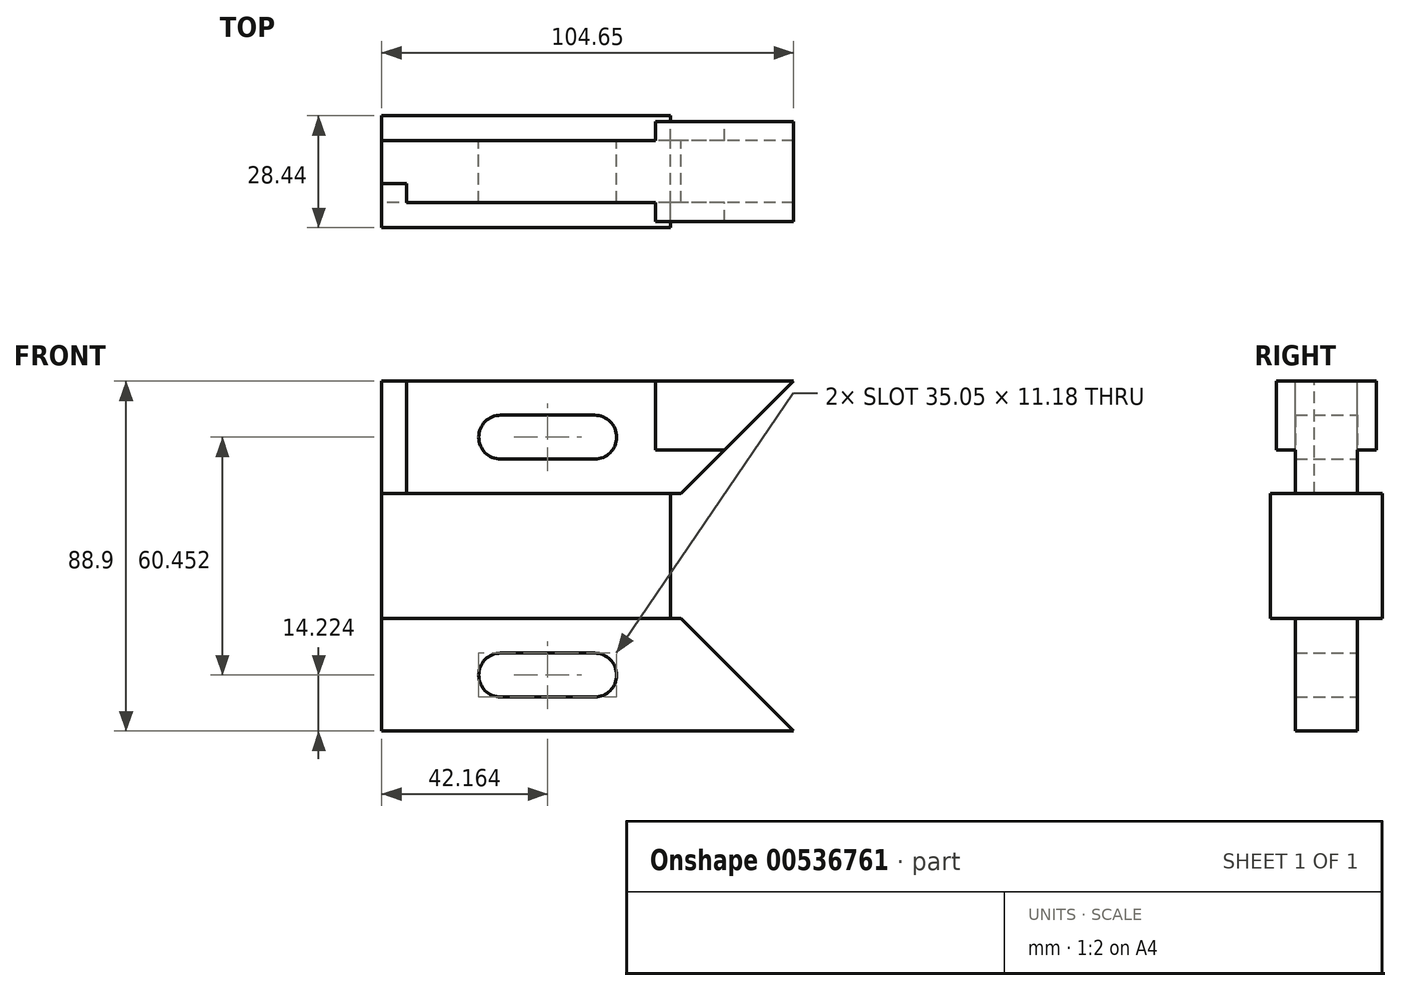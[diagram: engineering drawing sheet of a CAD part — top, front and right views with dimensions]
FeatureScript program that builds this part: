
annotation { "Feature Type Name" : "Feature", "Feature Type Description" : "" }
export const myFeature = defineFeature(function(context is Context, id is Id, definition is map)
    precondition{}
    {
        {
            var Q0;
            Q0=qCreatedBy(makeId("Right.planeOp"),FACE);
            var sketch = newSketch(context, id + "F0", { "sketchPlane" : qUnion([Q0])});
            skLineSegment(sketch, "E0.bottom", {"start": v(-14.22, 15.88) * mm, "end": v(14.22, 15.88) * mm});
            skLineSegment(sketch, "E0.top", {"start": v(-14.22, -15.87) * mm, "end": v(14.22, -15.87) * mm});
            skLineSegment(sketch, "E0.left", {"start": v(-14.22, 15.88) * mm, "end": v(-14.22, -15.87) * mm});
            skLineSegment(sketch, "E0.right", {"start": v(14.22, 15.88) * mm, "end": v(14.22, -15.87) * mm});
            skPoint(sketch, "E0.middle", {"position": v(0, 0) * mm});
            skSolve(sketch);
        }
        {
            var Q0;
            Q0 = qSketchRegion(id + "F0", true);
            extrude(context, id + "F1", {"entities" : qUnion([Q0]), "depth" : 73.4 * mm, "offsetDistance" : 25.4 * mm});
        }
        {
            var Q0;
            Q0=qCreatedBy(makeId("Front.planeOp"),FACE);
            var sketch = newSketch(context, id + "F2", { "sketchPlane" : qUnion([Q0])});
            skLineSegment(sketch, "E1.0", {"start": v(76.07, 15.88) * mm, "end": v(0, 15.88) * mm});
            skLineSegment(sketch, "E2", {"start": v(0, 15.88) * mm, "end": v(0, 44.45) * mm});
            skLineSegment(sketch, "E3", {"start": v(0, 44.45) * mm, "end": v(104.65, 44.45) * mm});
            skLineSegment(sketch, "E4", {"start": v(104.65, 44.45) * mm, "end": v(76.07, 15.87) * mm});
            skPoint(sketch, "E5.centerSnap1", {"position": v(36.7, 15.88) * mm});
            skCircle(sketch, "E6", {"center": v(30.23, 30.23) * mm, "radius": 5.59 * mm});
            skCircle(sketch, "E7", {"center": v(54.1, 30.23) * mm, "radius": 5.59 * mm});
            skLineSegment(sketch, "E8", {"start": v(30.23, 35.81) * mm, "end": v(54.1, 35.81) * mm});
            skLineSegment(sketch, "E9", {"start": v(30.23, 24.64) * mm, "end": v(54.1, 24.64) * mm});
            skLineSegment(sketch, "E10.MirrorCS", {"start": v(0, -15.88) * mm, "end": v(0, -44.45) * mm});
            skLineSegment(sketch, "E11.MirrorCS", {"start": v(0, -44.45) * mm, "end": v(104.65, -44.45) * mm});
            skLineSegment(sketch, "E12.MirrorCS", {"start": v(104.65, -44.45) * mm, "end": v(76.07, -15.87) * mm});
            skCircle(sketch, "E13.MirrorC", {"center": v(54.1, -30.23) * mm, "radius": 5.59 * mm});
            skLineSegment(sketch, "E14.MirrorCS", {"start": v(30.23, -35.81) * mm, "end": v(54.1, -35.81) * mm});
            skCircle(sketch, "E15.MirrorC", {"center": v(30.23, -30.23) * mm, "radius": 5.59 * mm});
            skLineSegment(sketch, "E16.MirrorCS", {"start": v(30.23, -24.64) * mm, "end": v(54.1, -24.64) * mm});
            skPoint(sketch, "E17.orphan", {"position": v(73.4, 15.88) * mm});
            skLineSegment(sketch, "E18.MirrorCS", {"start": v(76.07, -15.88) * mm, "end": v(0, -15.88) * mm});
            skSolve(sketch);
        }
        {
            var Q0;
            Q0=makeQuery(id+"F2.imprint","IMPRINT",FACE,{"disambiguationData":[TD([[makeQuery(id+"F2.imprint","IMPRINT",EDGE,{"derivedFrom":sQuery(id+"F2.wireOp",EDGE,"E1.0")}),-1.0]])]});
            var Q1;
            Q1=makeQuery(id+"F2.imprint","IMPRINT",FACE,{"disambiguationData":[TD([[makeQuery(id+"F2.imprint","IMPRINT",EDGE,{"derivedFrom":sQuery(id+"F2.wireOp",EDGE,"E10.MirrorCS")}),1.0]])]});
            extrude(context, id + "F3", {"entities" : qUnion([Q0, Q1]), "operationType" : NewBodyOperationType.ADD, "endBound" : BoundingType.SYMMETRIC, "depth" : 15.75 * mm, "offsetDistance" : 25.4 * mm});
        }
        {
            var Q0;
            Q0=makeQuery(id+"F3.opExtrude","CAP_FACE",FACE,{"disambiguationData":[OSD([sQuery(id+"F2.wireOp",EDGE,"E1.0"),sQuery(id+"F2.wireOp",EDGE,"E2"),sQuery(id+"F2.wireOp",EDGE,"E3"),sQuery(id+"F2.wireOp",EDGE,"E4"),sQuery(id+"F2.wireOp",EDGE,"E6"),sQuery(id+"F2.wireOp",EDGE,"E7"),sQuery(id+"F2.wireOp",EDGE,"E8"),sQuery(id+"F2.wireOp",EDGE,"E9")])],"isStart":false});
            var sketch = newSketch(context, id + "F4", { "sketchPlane" : qUnion([Q0])});
            skLineSegment(sketch, "E19.bottom", {"start": v(0, 15.88) * mm, "end": v(6.35, 15.88) * mm});
            skLineSegment(sketch, "E19.top", {"start": v(0, 44.45) * mm, "end": v(6.35, 44.45) * mm});
            skLineSegment(sketch, "E19.left", {"start": v(0, 15.88) * mm, "end": v(0, 44.45) * mm});
            skLineSegment(sketch, "E19.right", {"start": v(6.35, 15.88) * mm, "end": v(6.35, 44.45) * mm});
            skSolve(sketch);
        }
        {
            var Q0;
            Q0=makeQuery(id+"F4.imprint","IMPRINT",FACE,{"disambiguationData":[TD([[makeQuery(id+"F4.imprint","IMPRINT",EDGE,{"derivedFrom":sQuery(id+"F4.wireOp",EDGE,"E19.bottom")}),-1.0]])]});
            extrude(context, id + "F5", {"entities" : qUnion([Q0]), "operationType" : NewBodyOperationType.REMOVE, "oppositeDirection" : true, "depth" : 4.83 * mm, "offsetDistance" : 25.4 * mm});
        }
        {
            var Q0;
            Q0=qCreatedBy(makeId("Front.planeOp"),FACE);
            var sketch = newSketch(context, id + "F6", { "sketchPlane" : qUnion([Q0])});
            skLineSegment(sketch, "E20.0", {"start": v(6.35, 44.45) * mm, "end": v(104.65, 44.45) * mm});
            skLineSegment(sketch, "E21.0", {"start": v(104.65, 44.45) * mm, "end": v(76.07, 15.87) * mm});
            skLineSegment(sketch, "E22", {"start": v(69.6, 44.45) * mm, "end": v(69.6, 26.92) * mm});
            skLineSegment(sketch, "E23", {"start": v(69.6, 26.92) * mm, "end": v(87.12, 26.92) * mm});
            skSolve(sketch);
        }
        {
            var Q0;
            Q0 = qSketchRegion(id + "F6", true);
            extrude(context, id + "F7", {"entities" : qUnion([Q0]), "operationType" : NewBodyOperationType.ADD, "endBound" : BoundingType.SYMMETRIC, "depth" : 25.4 * mm, "offsetDistance" : 25.4 * mm});
        }
    });
